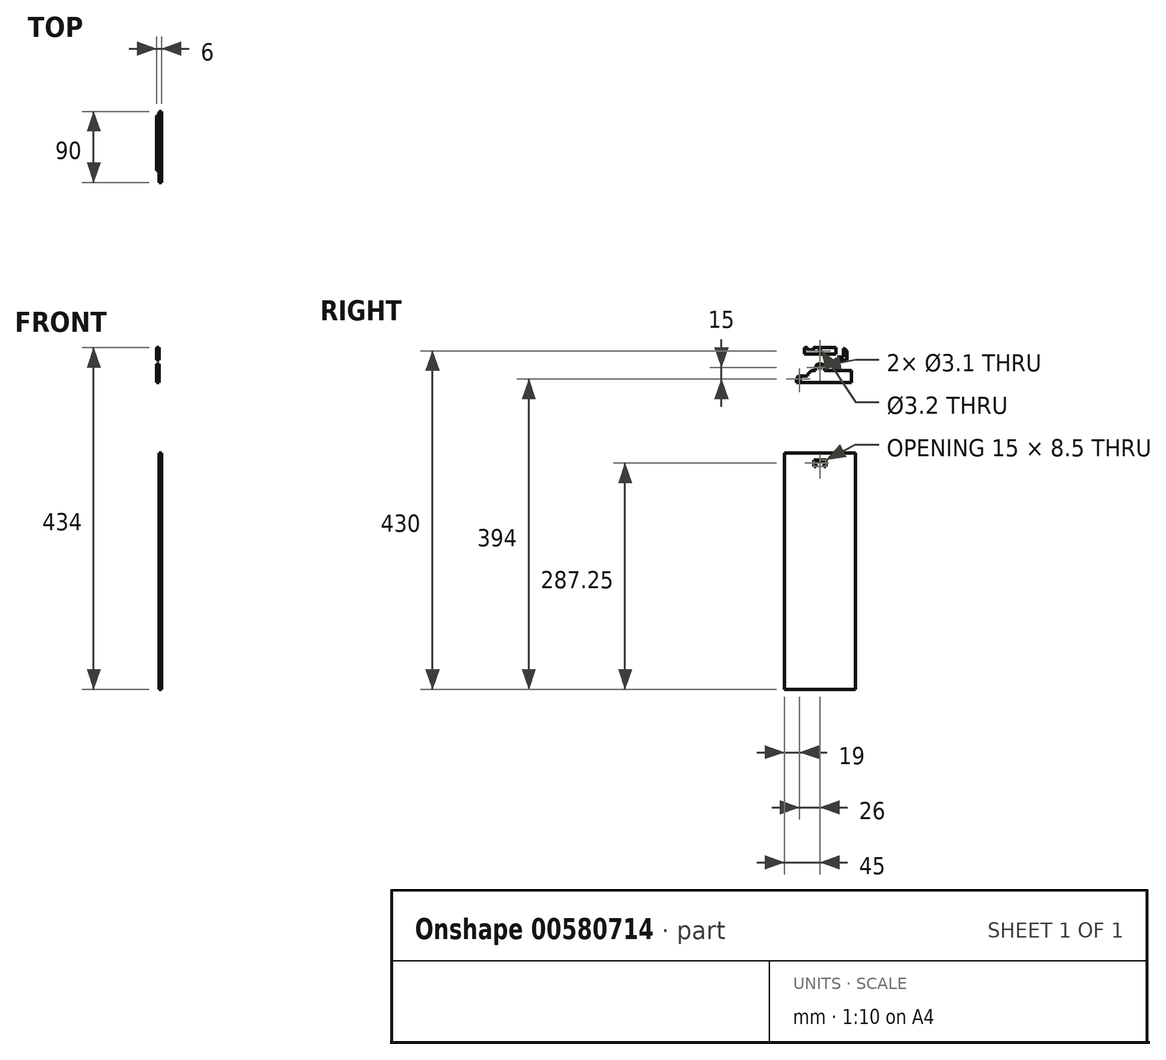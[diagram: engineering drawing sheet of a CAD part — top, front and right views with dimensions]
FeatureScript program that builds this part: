
annotation { "Feature Type Name" : "Feature", "Feature Type Description" : "" }
export const myFeature = defineFeature(function(context is Context, id is Id, definition is map)
    precondition{}
    {
        {
            var Q0;
            Q0=qCreatedBy(makeId("Right.planeOp"),FACE);
            var sketch = newSketch(context, id + "F0", { "sketchPlane" : qUnion([Q0])});
            skLineSegment(sketch, "E0.bottom", {"start": v(-30, 15) * mm, "end": v(40, 15) * mm});
            skLineSegment(sketch, "E0.top", {"start": v(-30, 0) * mm, "end": v(40, 0) * mm});
            skLineSegment(sketch, "E0.left", {"start": v(-30, 15) * mm, "end": v(-30, 0) * mm});
            skLineSegment(sketch, "E0.right", {"start": v(40, 15) * mm, "end": v(40, 0) * mm});
            skLineSegment(sketch, "E1.bottom", {"start": v(-6, 23) * mm, "end": v(6, 23) * mm});
            skLineSegment(sketch, "E1.top", {"start": v(-6, 15) * mm, "end": v(6, 15) * mm});
            skLineSegment(sketch, "E1.left", {"start": v(-6, 23) * mm, "end": v(-6, 15) * mm});
            skLineSegment(sketch, "E1.right", {"start": v(6, 23) * mm, "end": v(6, 15) * mm});
            skCircle(sketch, "E2", {"center": v(0, 19) * mm, "radius": 1.55 * mm});
            skCircle(sketch, "E3", {"center": v(-26, 4) * mm, "radius": 1.55 * mm});
            skLineSegment(sketch, "E4.bottom", {"start": v(-30, 15) * mm, "end": v(-16, 15) * mm});
            skLineSegment(sketch, "E4.top", {"start": v(-30, 8) * mm, "end": v(-16, 8) * mm});
            skLineSegment(sketch, "E4.left", {"start": v(-30, 15) * mm, "end": v(-30, 8) * mm});
            skLineSegment(sketch, "E4.right", {"start": v(-16, 15) * mm, "end": v(-16, 8) * mm});
            skSolve(sketch);
        }
        {
            var Q0;
            Q0=makeQuery(id+"F0.imprint","IMPRINT",FACE,{"disambiguationData":[TD([[makeQuery(id+"F0.imprint","IMPRINT",EDGE,{"derivedFrom":sQuery(id+"F0.wireOp",EDGE,"E0.top")}),1.0]])]});
            var Q1;
            Q1=makeQuery(id+"F0.imprint","IMPRINT",FACE,{"disambiguationData":[TD([[makeQuery(id+"F0.imprint","IMPRINT",EDGE,{"derivedFrom":sQuery(id+"F0.wireOp",EDGE,"E1.bottom")}),-1.0]])]});
            extrude(context, id + "F1", {"entities" : qUnion([Q0, Q1]), "depth" : 3 * mm, "offsetDistance" : 25 * mm});
        }
        {
            var Q0;
            Q0=qCreatedBy(makeId("Right.planeOp"),FACE);
            var sketch = newSketch(context, id + "F2", { "sketchPlane" : qUnion([Q0])});
            skLineSegment(sketch, "E5.bottom", {"start": v(-20, 44) * mm, "end": v(20, 44) * mm});
            skLineSegment(sketch, "E5.top", {"start": v(-20, 36) * mm, "end": v(20, 36) * mm});
            skLineSegment(sketch, "E5.left", {"start": v(-20, 44) * mm, "end": v(-20, 36) * mm});
            skLineSegment(sketch, "E5.right", {"start": v(20, 44) * mm, "end": v(20, 36) * mm});
            skLineSegment(sketch, "E6.bottom", {"start": v(20, 36) * mm, "end": v(10, 36) * mm});
            skLineSegment(sketch, "E6.top", {"start": v(20, 28) * mm, "end": v(10, 28) * mm});
            skLineSegment(sketch, "E6.left", {"start": v(20, 36) * mm, "end": v(20, 28) * mm});
            skLineSegment(sketch, "E6.right", {"start": v(10, 36) * mm, "end": v(10, 28) * mm});
            skLineSegment(sketch, "E7.bottom", {"start": v(20, 28) * mm, "end": v(30, 28) * mm});
            skLineSegment(sketch, "E7.top", {"start": v(20, 32) * mm, "end": v(30, 32) * mm});
            skLineSegment(sketch, "E7.left", {"start": v(20, 28) * mm, "end": v(20, 32) * mm});
            skLineSegment(sketch, "E7.right", {"start": v(30, 28) * mm, "end": v(30, 32) * mm});
            skLineSegment(sketch, "E8.bottom", {"start": v(30, 28) * mm, "end": v(34, 28) * mm});
            skLineSegment(sketch, "E8.top", {"start": v(30, 43) * mm, "end": v(34, 43) * mm});
            skLineSegment(sketch, "E8.left", {"start": v(30, 28) * mm, "end": v(30, 43) * mm});
            skLineSegment(sketch, "E8.right", {"start": v(34, 28) * mm, "end": v(34, 43) * mm});
            skLineSegment(sketch, "E9.bottom", {"start": v(-16, 44) * mm, "end": v(-8, 44) * mm});
            skLineSegment(sketch, "E9.top", {"start": v(-16, 41) * mm, "end": v(-8, 41) * mm});
            skLineSegment(sketch, "E9.left", {"start": v(-16, 44) * mm, "end": v(-16, 41) * mm});
            skLineSegment(sketch, "E9.right", {"start": v(-8, 44) * mm, "end": v(-8, 41) * mm});
            skCircle(sketch, "E10", {"center": v(0, 40) * mm, "radius": 1.6 * mm});
            skSolve(sketch);
        }
        {
            var Q0;
            Q0=makeQuery(id+"F2.imprint","IMPRINT",FACE,{"disambiguationData":[TD([[makeQuery(id+"F2.imprint","IMPRINT",EDGE,{"derivedFrom":sQuery(id+"F2.wireOp",EDGE,"E5.top")}),1.0]])]});
            var Q1;
            Q1=makeQuery(id+"F2.imprint","IMPRINT",FACE,{"disambiguationData":[TD([[makeQuery(id+"F2.imprint","IMPRINT",EDGE,{"derivedFrom":sQuery(id+"F2.wireOp",EDGE,"E6.bottom")}),1.0]])]});
            var Q2;
            {var subQ0=sQuery(id+"F2.wireOp",EDGE,"E7.bottom");Q2=makeQuery(id+"F2.imprint","IMPRINT",FACE,{"disambiguationData":[TD([[makeQuery(id+"F2.imprint","IMPRINT",EDGE,{"derivedFrom":subQ0}),1.0]])]});}
            var Q3;
            {var subQ3=sQuery(id+"F2.wireOp",EDGE,"E8.bottom");Q3=makeQuery(id+"F2.imprint","IMPRINT",FACE,{"disambiguationData":[TD([[makeQuery(id+"F2.imprint","IMPRINT",EDGE,{"derivedFrom":subQ3}),1.0]])]});}
            extrude(context, id + "F3", {"entities" : qUnion([Q0, Q1, Q2, Q3]), "depth" : 3 * mm, "offsetDistance" : 25 * mm});
        }
        {
            var Q0;
            Q0=makeQuery(id+"F1.opExtrude","SWEPT_EDGE",EDGE,{"disambiguationData":[OSD([sQuery(id+"F0.wireOp",EDGE,"E1.bottom"),sQuery(id+"F0.wireOp",EDGE,"E1.left")])]});
            var Q1;
            Q1=makeQuery(id+"F1.opExtrude","SWEPT_EDGE",EDGE,{"disambiguationData":[OSD([sQuery(id+"F0.wireOp",EDGE,"E1.bottom"),sQuery(id+"F0.wireOp",EDGE,"E1.right")])]});
            chamfer(context, id + "F4", {"entities" : qUnion([Q0, Q1]), "width" : 3 * mm, "tangentPropagation" : true});
        }
        {
            var Q0;
            Q0=makeQuery(id+"F3.opExtrude","SWEPT_EDGE",EDGE,{"disambiguationData":[OSD([sQuery(id+"F2.wireOp",EDGE,"E6.top"),sQuery(id+"F2.wireOp",EDGE,"E6.right")])]});
            chamfer(context, id + "F5", {"entities" : qUnion([Q0]), "width" : 6 * mm, "tangentPropagation" : true});
        }
        {
            var Q0;
            Q0=makeQuery(id+"F3.opExtrude","SWEPT_EDGE",EDGE,{"disambiguationData":[OSD([sQuery(id+"F2.wireOp",EDGE,"E8.top"),sQuery(id+"F2.wireOp",EDGE,"E8.right")])]});
            chamfer(context, id + "F6", {"entities" : qUnion([Q0]), "width" : 3 * mm, "tangentPropagation" : true});
        }
        {
            var Q0;
            Q0=makeQuery(id+"F1.opExtrude","SWEPT_EDGE",EDGE,{"disambiguationData":[OSD([sQuery(id+"F0.wireOp",EDGE,"E0.bottom"),sQuery(id+"F0.wireOp",EDGE,"E4.bottom"),sQuery(id+"F0.wireOp",EDGE,"E4.right")])]});
            chamfer(context, id + "F7", {"entities" : qUnion([Q0]), "width" : 5 * mm, "tangentPropagation" : true});
        }
        {
            var Q0;
            Q0=makeQuery(id+"F1.opExtrude","SWEPT_EDGE",EDGE,{"disambiguationData":[OSD([sQuery(id+"F0.wireOp",EDGE,"E0.left"),sQuery(id+"F0.wireOp",EDGE,"E4.top"),sQuery(id+"F0.wireOp",EDGE,"E4.left")])]});
            chamfer(context, id + "F8", {"entities" : qUnion([Q0]), "width" : 3 * mm, "tangentPropagation" : true});
        }
        {
            var Q0;
            Q0=makeQuery(id+"F1.opExtrude","CAP_FACE",FACE,{"disambiguationData":[OSD([sQuery(id+"F0.wireOp",EDGE,"E0.bottom"),sQuery(id+"F0.wireOp",EDGE,"E0.top"),sQuery(id+"F0.wireOp",EDGE,"E0.left"),sQuery(id+"F0.wireOp",EDGE,"E0.right"),sQuery(id+"F0.wireOp",EDGE,"E1.bottom"),sQuery(id+"F0.wireOp",EDGE,"E1.left"),sQuery(id+"F0.wireOp",EDGE,"E1.right"),sQuery(id+"F0.wireOp",EDGE,"E2"),sQuery(id+"F0.wireOp",EDGE,"E3"),sQuery(id+"F0.wireOp",EDGE,"E4.top"),sQuery(id+"F0.wireOp",EDGE,"E4.right")])],"isStart":false});
            var sketch = newSketch(context, id + "F9", { "sketchPlane" : qUnion([Q0])});
            skLineSegment(sketch, "E11.bottom", {"start": v(45, -90) * mm, "end": v(-45, -90) * mm});
            skLineSegment(sketch, "E11.top", {"start": v(45, -390) * mm, "end": v(-45, -390) * mm});
            skLineSegment(sketch, "E11.left", {"start": v(45, -90) * mm, "end": v(45, -390) * mm});
            skLineSegment(sketch, "E11.right", {"start": v(-45, -90) * mm, "end": v(-45, -390) * mm});
            skPoint(sketch, "E11.middle", {"position": v(0, -240) * mm});
            skLineSegment(sketch, "E12.bottom", {"start": v(7.5, -98.5) * mm, "end": v(-7.5, -98.5) * mm});
            skLineSegment(sketch, "E12.top", {"start": v(7.5, -101.5) * mm, "end": v(-7.5, -101.5) * mm});
            skLineSegment(sketch, "E12.left", {"start": v(7.5, -98.5) * mm, "end": v(7.5, -101.5) * mm});
            skLineSegment(sketch, "E12.right", {"start": v(-7.5, -98.5) * mm, "end": v(-7.5, -101.5) * mm});
            skPoint(sketch, "E12.middle", {"position": v(0, -100) * mm});
            skLineSegment(sketch, "E13.bottom", {"start": v(5, -104.5) * mm, "end": v(7.5, -104.5) * mm});
            skLineSegment(sketch, "E13.top", {"start": v(5, -107) * mm, "end": v(7.5, -107) * mm});
            skLineSegment(sketch, "E13.left", {"start": v(5, -104.5) * mm, "end": v(5, -107) * mm});
            skLineSegment(sketch, "E13.right", {"start": v(7.5, -104.5) * mm, "end": v(7.5, -107) * mm});
            skLineSegment(sketch, "E14", {"start": v(6, -101.5) * mm, "end": v(6.25, -104.5) * mm});
            skLineSegment(sketch, "E15", {"start": v(7, -101.5) * mm, "end": v(7.5, -104.5) * mm});
            skLineSegment(sketch, "E16.MirrorCS", {"start": v(-5, -104.5) * mm, "end": v(-7.5, -104.5) * mm});
            skLineSegment(sketch, "E17.MirrorCS", {"start": v(-5, -107) * mm, "end": v(-7.5, -107) * mm});
            skLineSegment(sketch, "E18.MirrorCS", {"start": v(-7.5, -104.5) * mm, "end": v(-7.5, -107) * mm});
            skLineSegment(sketch, "E19.MirrorCS", {"start": v(-7, -101.5) * mm, "end": v(-7.5, -104.5) * mm});
            skLineSegment(sketch, "E20.MirrorCS", {"start": v(-5, -104.5) * mm, "end": v(-5, -107) * mm});
            skLineSegment(sketch, "E21.MirrorCS", {"start": v(-6, -101.5) * mm, "end": v(-6.25, -104.5) * mm});
            skLineSegment(sketch, "E22.MirrorCS", {"start": v(-7.5, -98.5) * mm, "end": v(7.5, -98.5) * mm});
            skLineSegment(sketch, "E23.MirrorCS", {"start": v(-7.5, -101.5) * mm, "end": v(7.5, -101.5) * mm});
            skSolve(sketch);
        }
        {
            var Q0;
            Q0=makeQuery(id+"F9.imprint","IMPRINT",FACE,{"disambiguationData":[TD([[makeQuery(id+"F9.imprint","IMPRINT",EDGE,{"derivedFrom":sQuery(id+"F9.wireOp",EDGE,"E11.bottom")}),1.0]])]});
            extrude(context, id + "F10", {"entities" : qUnion([Q0]), "depth" : 3 * mm, "offsetDistance" : 25 * mm});
        }
    });
